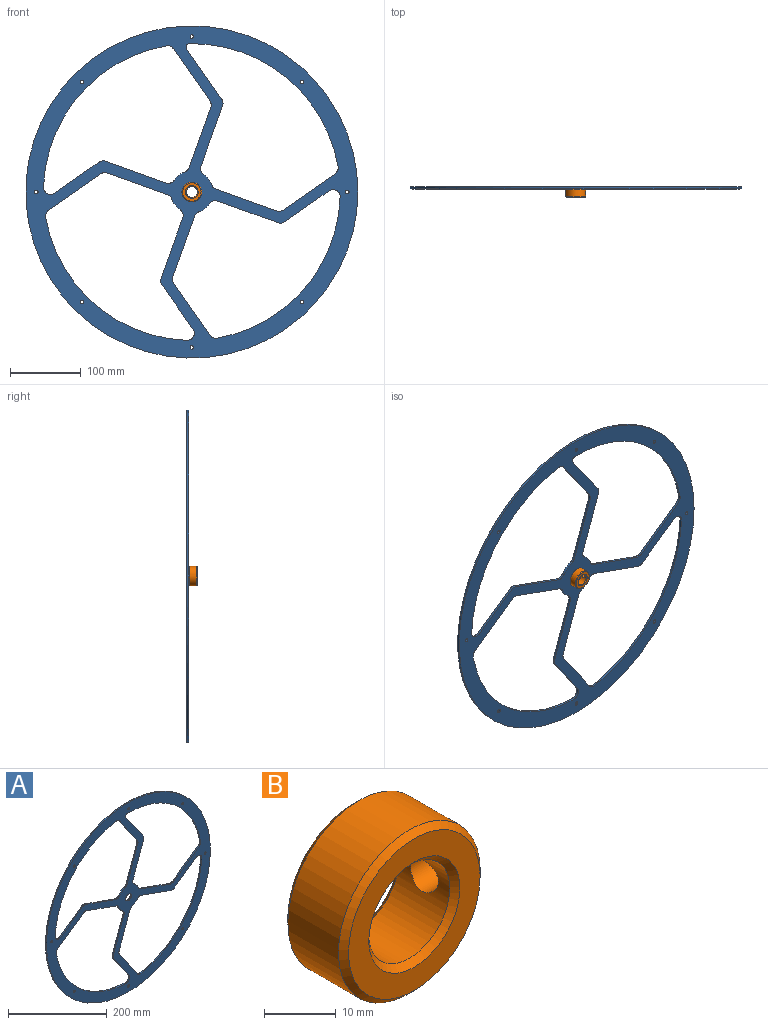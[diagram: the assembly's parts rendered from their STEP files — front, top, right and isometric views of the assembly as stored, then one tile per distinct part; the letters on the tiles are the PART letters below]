
ASSEMBLY  parts=2 mates=1
PART A: 60 faces, bbox 470x3x470 mm
  f0: cylinder r=10mm len=9.9mm, axis (0,1,0), area 34mm2, adj f1,f44,f58,f59
  f1: plane 73.72x51.62mm, normal (0.82,0,0.57), area 270mm2, adj f0,f2,f58,f59
  f2: cylinder r=10mm len=9.11mm, axis (0,1,0), area 28.7mm2, adj f1,f3,f58,f59
  f3: plane 85.6x30.7mm, normal (0.94,0,-0.34), area 272.8mm2, adj f2,f4,f58,f59
  f4: cylinder r=10mm len=6.09mm, axis (0,1,0), area 26.6mm2, adj f3,f5,f58,f59
  f5: cylinder r=30mm len=14.95mm, axis (0,1,0), area 57.7mm2, adj f4,f6,f58,f59
  f6: cylinder r=10mm len=11.68mm, axis (0,1,0), area 39.7mm2, adj f5,f7,f58,f59
  f7: plane 85.6x30.7mm, normal (-0.34,0,-0.94), area 272.8mm2, adj f6,f8,f58,f59
  f8: cylinder r=10mm len=9.11mm, axis (0,1,0), area 28.7mm2, adj f7,f9,f58,f59
  f9: plane 62.85x44.01mm, normal (0.57,0,-0.82), area 230.2mm2, adj f8,f10,f58,f59
  f10: cylinder r=10mm len=15.74mm, axis (0,1,0), area 66.4mm2, adj f9,f44,f58,f59
  f11: cylinder r=10mm len=6.09mm, axis (0,1,0), area 26.6mm2, adj f12,f45,f58,f59
  f12: cylinder r=30mm len=14.95mm, axis (0,1,0), area 57.7mm2, adj f11,f13,f58,f59
  f13: cylinder r=10mm len=11.68mm, axis (0,1,0), area 39.7mm2, adj f12,f14,f58,f59
  f14: plane 85.6x30.7mm, normal (0.94,0,-0.34), area 272.8mm2, adj f13,f15,f58,f59
  f15: cylinder r=10mm len=9.11mm, axis (0,1,0), area 28.7mm2, adj f14,f16,f58,f59
  f16: plane 70.8x49.57mm, normal (0.82,0,0.57), area 259.3mm2, adj f15,f17,f58,f59
  f17: cylinder r=5mm len=7.87mm, axis (0,1,0), area 32.5mm2, adj f16,f18,f58,f59
  f18: cylinder r=210mm len=210.12mm, axis (0,1,0), area 890.9mm2, adj f17,f19,f58,f59
  f19: cylinder r=10mm len=9.9mm, axis (0,1,0), area 34mm2, adj f18,f20,f58,f59
  f20: plane 73.72x51.62mm, normal (-0.57,0,0.82), area 270mm2, adj f19,f21,f58,f59
  f21: cylinder r=10mm len=9.11mm, axis (0,1,0), area 28.7mm2, adj f20,f45,f58,f59
  f22: cylinder r=10mm len=9.11mm, axis (0,1,0), area 28.7mm2, adj f23,f46,f58,f59
  f23: plane 62.85x44.01mm, normal (-0.57,0,0.82), area 230.2mm2, adj f22,f24,f58,f59
  f24: cylinder r=10mm len=15.74mm, axis (0,1,0), area 66.4mm2, adj f23,f25,f58,f59
  f25: cylinder r=210mm len=200.05mm, axis (0,1,0), area 860.7mm2, adj f24,f26,f58,f59
  f26: cylinder r=10mm len=9.9mm, axis (0,1,0), area 34mm2, adj f25,f27,f58,f59
  f27: plane 73.72x51.62mm, normal (-0.82,0,-0.57), area 270mm2, adj f26,f28,f58,f59
  f28: cylinder r=10mm len=9.11mm, axis (0,1,0), area 28.7mm2, adj f27,f29,f58,f59
  f29: plane 85.6x30.7mm, normal (-0.94,0,0.34), area 272.8mm2, adj f28,f30,f58,f59
  f30: cylinder r=10mm len=6.09mm, axis (0,1,0), area 26.6mm2, adj f29,f31,f58,f59
  f31: cylinder r=30mm len=14.95mm, axis (0,1,0), area 57.7mm2, adj f30,f32,f58,f59
  f32: cylinder r=10mm len=11.68mm, axis (0,1,0), area 39.7mm2, adj f31,f46,f58,f59
  f33: cylinder r=10mm len=11.68mm, axis (0,1,0), area 39.7mm2, adj f34,f47,f58,f59
  f34: plane 85.6x30.7mm, normal (-0.94,0,0.34), area 272.8mm2, adj f33,f35,f58,f59
  f35: cylinder r=10mm len=9.11mm, axis (0,1,0), area 28.7mm2, adj f34,f36,f58,f59
  f36: plane 62.85x44.01mm, normal (-0.82,0,-0.57), area 230.2mm2, adj f35,f37,f58,f59
  f37: cylinder r=10mm len=15.74mm, axis (0,1,0), area 66.4mm2, adj f36,f38,f58,f59
  f38: cylinder r=210mm len=200.05mm, axis (0,1,0), area 860.7mm2, adj f37,f39,f58,f59
  f39: cylinder r=10mm len=9.9mm, axis (0,1,0), area 34mm2, adj f38,f40,f58,f59
  f40: plane 73.72x51.62mm, normal (0.57,0,-0.82), area 270mm2, adj f39,f41,f58,f59
  f41: cylinder r=10mm len=9.11mm, axis (0,1,0), area 28.7mm2, adj f40,f42,f58,f59
  f42: plane 85.6x30.7mm, normal (-0.34,0,-0.94), area 272.8mm2, adj f41,f43,f58,f59
  f43: cylinder r=10mm len=6.09mm, axis (0,1,0), area 26.6mm2, adj f42,f47,f58,f59
  f44: cylinder r=210mm len=200.05mm, axis (0,1,0), area 860.7mm2, adj f0,f10,f58,f59
  f45: plane 85.6x30.7mm, normal (0.34,0,0.94), area 272.8mm2, adj f11,f21,f58,f59
  f46: plane 85.6x30.7mm, normal (0.34,0,0.94), area 272.8mm2, adj f22,f32,f58,f59
  f47: cylinder r=30mm len=14.95mm, axis (0,1,0), area 57.7mm2, adj f33,f43,f58,f59
  f48: cylinder r=2.5mm len=5mm, axis (0,1,0), area 47.1mm2, adj f58,f59
  f49: cylinder r=2.5mm len=5mm, axis (0,1,0), area 47.1mm2, adj f58,f59
  f50: cylinder r=2.5mm len=5mm, axis (0,1,0), area 47.1mm2, adj f58,f59
  f51: cylinder r=2.5mm len=5mm, axis (0,1,0), area 47.1mm2, adj f58,f59
  f52: cylinder r=8mm len=16mm, axis (0,1,0), area 150.8mm2, adj f58,f59
  f53: cylinder r=2.5mm len=5mm, axis (0,1,0), area 47.1mm2, adj f58,f59
  f54: cylinder r=2.5mm len=5mm, axis (0,1,0), area 47.1mm2, adj f58,f59
  f55: cylinder r=2.5mm len=5mm, axis (0,1,0), area 47.1mm2, adj f58,f59
  f56: cylinder r=2.5mm len=5mm, axis (0,1,0), area 47.1mm2, adj f58,f59
  f57: cylinder r=235mm len=470mm, axis (0,1,0), area 4429.6mm2, adj f58,f59
  f58: plane 470x470mm, normal (0,-1,0), area 50005.3mm2, adj f0,f1,f2,f3,f4,f5,f6,f7
  f59: plane 470x470mm, normal (0,1,0), area 50005.3mm2, adj f0,f1,f2,f3,f4,f5,f6,f7
PART B: 9 faces, bbox 28x12x28 mm
  f0: cylinder r=8mm len=16mm, axis (0,1,0), area 478.6mm2, adj f4,f5,f8
  f1: cylinder r=14mm len=28mm, axis (0,1,0), area 855.9mm2, adj f6,f7,f8
  f2: plane 26x26mm, normal (0,-1,0), area 276.5mm2, adj f4,f6
  f3: plane 26x26mm, normal (0,1,0), area 276.5mm2, adj f5,f7
  f4: cone r=8mm half-angle=45deg, axis (0,-1,0), area 75.5mm2, adj f0,f2
  f5: cone r=9mm half-angle=45deg, axis (0,1,0), area 75.5mm2, adj f0,f3
  f6: cone r=13mm half-angle=45deg, axis (0,1,0), area 120mm2, adj f1,f2
  f7: cone r=14mm half-angle=45deg, axis (0,-1,0), area 120mm2, adj f1,f3
  f8: cylinder r=2.75mm len=6.49mm, axis (1,0,0), area 105.5mm2, adj f0,f1
PLACE A t=(159.16,-524,-317.8)mm fixed
PLACE B t=(159.16,-527,-317.8)mm
MATE fastened A.f5 <-> B.f0  axis (0,-1,0) through (159.16,-527,-317.8)mm
